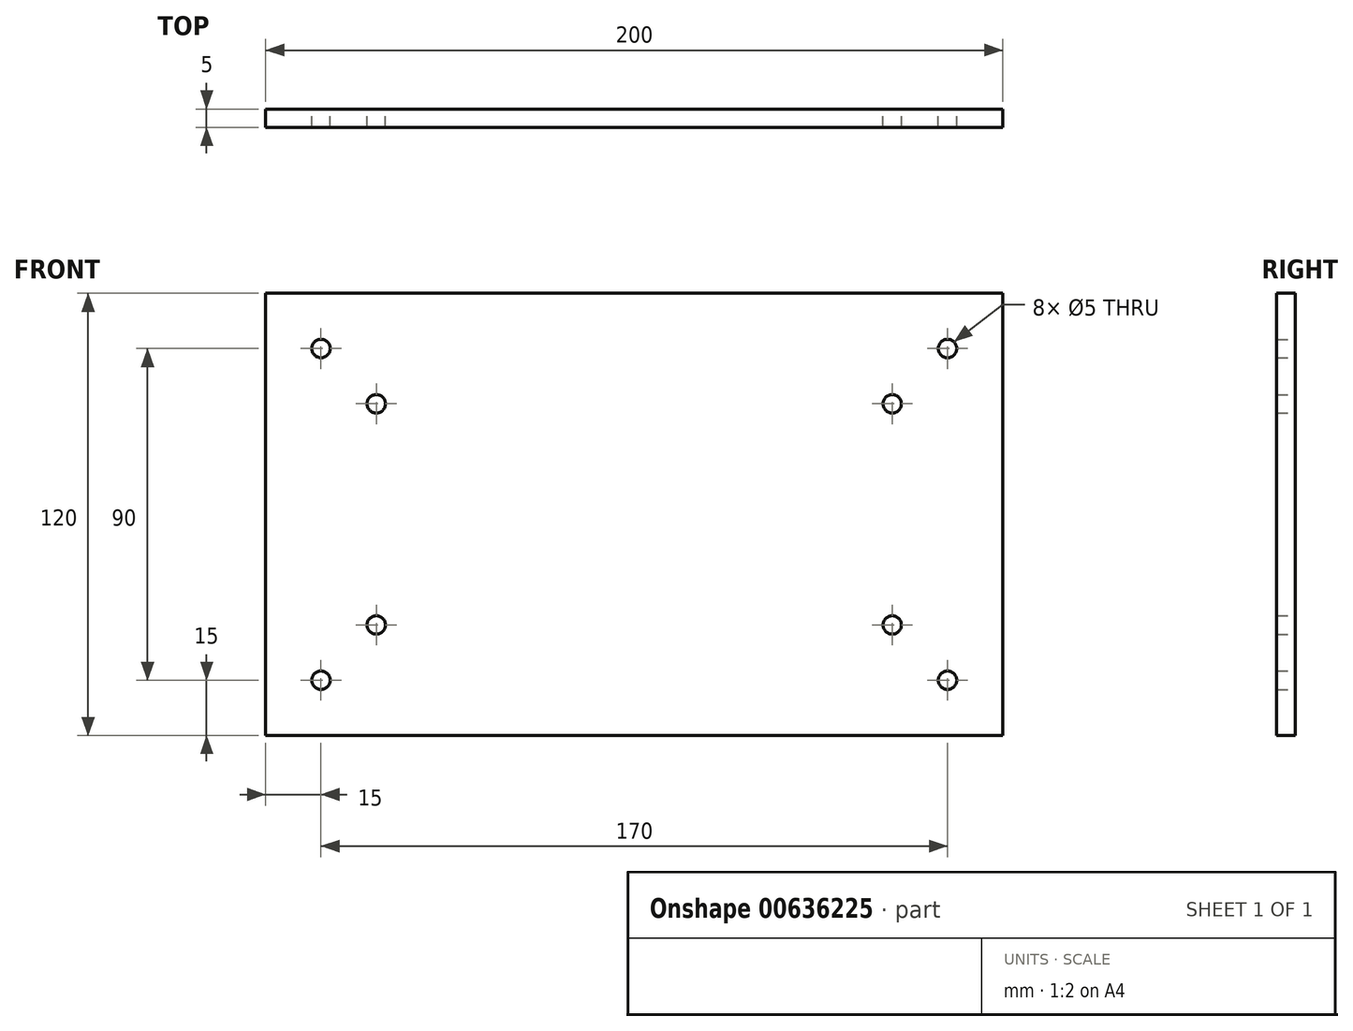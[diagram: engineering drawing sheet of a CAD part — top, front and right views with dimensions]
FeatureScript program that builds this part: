
annotation { "Feature Type Name" : "Feature", "Feature Type Description" : "" }
export const myFeature = defineFeature(function(context is Context, id is Id, definition is map)
    precondition{}
    {
        {
            var Q0;
            Q0=qCreatedBy(makeId("Front.planeOp"),FACE);
            var sketch = newSketch(context, id + "F0", { "sketchPlane" : qUnion([Q0])});
            skLineSegment(sketch, "E0.bottom", {"start": v(0, 0) * mm, "end": v(200, 0) * mm});
            skLineSegment(sketch, "E0.top", {"start": v(0, 120) * mm, "end": v(200, 120) * mm});
            skLineSegment(sketch, "E0.left", {"start": v(0, 0) * mm, "end": v(0, 120) * mm});
            skLineSegment(sketch, "E0.right", {"start": v(200, 0) * mm, "end": v(200, 120) * mm});
            skCircle(sketch, "E1", {"center": v(185, 105) * mm, "radius": 2.5 * mm});
            skCircle(sketch, "E2", {"center": v(170, 90) * mm, "radius": 2.5 * mm});
            skCircle(sketch, "E3", {"center": v(185, 15) * mm, "radius": 2.5 * mm});
            skCircle(sketch, "E4", {"center": v(170, 30) * mm, "radius": 2.5 * mm});
            skCircle(sketch, "E5.MirrorC", {"center": v(30, 90) * mm, "radius": 2.5 * mm});
            skCircle(sketch, "E6.MirrorC", {"center": v(30, 30) * mm, "radius": 2.5 * mm});
            skCircle(sketch, "E7.MirrorC", {"center": v(15, 105) * mm, "radius": 2.5 * mm});
            skCircle(sketch, "E8.MirrorC", {"center": v(15, 15) * mm, "radius": 2.5 * mm});
            skSolve(sketch);
        }
        {
            var Q0;
            Q0=makeQuery(id+"F0.imprint","IMPRINT",FACE,{"disambiguationData":[TD([[makeQuery(id+"F0.imprint","IMPRINT",EDGE,{"derivedFrom":sQuery(id+"F0.wireOp",EDGE,"E0.bottom")}),1.0]])]});
            extrude(context, id + "F1", {"entities" : qUnion([Q0]), "depth" : 5 * mm, "offsetDistance" : 25.4 * mm});
        }
    });
